# Revit family: Corridor PIR Sensor_341
name_source: partatom
category: Electrical Fixtures
revit_build: Autodesk Revit 2018 (Build: 20170223_1515(x64)
units: mm (PartAtom-declared; Revit-internal decimal feet)

## family parameters
Always vertical = Yes
Cut with Voids When Loaded = No
Maintain Annotation Orientation = No
Part Type = Normal
Room Calculation Point = No
Round Connector Dimension = Use Diameter
Shared = No
Work Plane-Based = Yes

## types (1)
- CORRIDOR PIR SENSOR
    Ambient temperature = 0 °C to +50 °C, greater than 5°C difference required
    Cable rating = All cables must be mains rated.
    DALI : = 4-way connector block
    DALI consumption: = 15 mA
    DALI supply input = 13 V – 22.5 V
    Default Elevation = 0 mm  [stored 0 ft]
    Designer = 4.1 or later
    Dimensions: = 70 mm × 102 mm × 50 mm
    EMC emission = EN 55015
    EMC immunity = EN 61547
    Environment = Complies with WEEE and RoHS directives.
    Finish / Colour: = Semi-matt / White RAL 9003
    IP code: = IP42
    Manufacturer = Helvar
    Material (casing): = UL94V-HB ABS
    Max reach = 41 m
    Max. recommended mounting height = 2.5 m
    Model = 341
    Presence detection coverage area = 1470 m² @ 2 m mounting height
    Relative humidity = Max. 90 %, noncondensing
    Safety = EN 60950
    Storage temperature = −10 °C to +70 °C
    Toolbox: = 2.2.12 or later
    Vertical adjustment: = −20° to +10°
    Weight = 93 g
    Wire section = 0.5 mm² – 1.5 mm² solid or stranded

note: [stored X ft] marks values corroborated as IEEE doubles in the binary element streams (Revit-internal decimal feet)

## geometry (parser evidence)
native form markers: Sweep x1
no freeform markers — native parametric forms only
